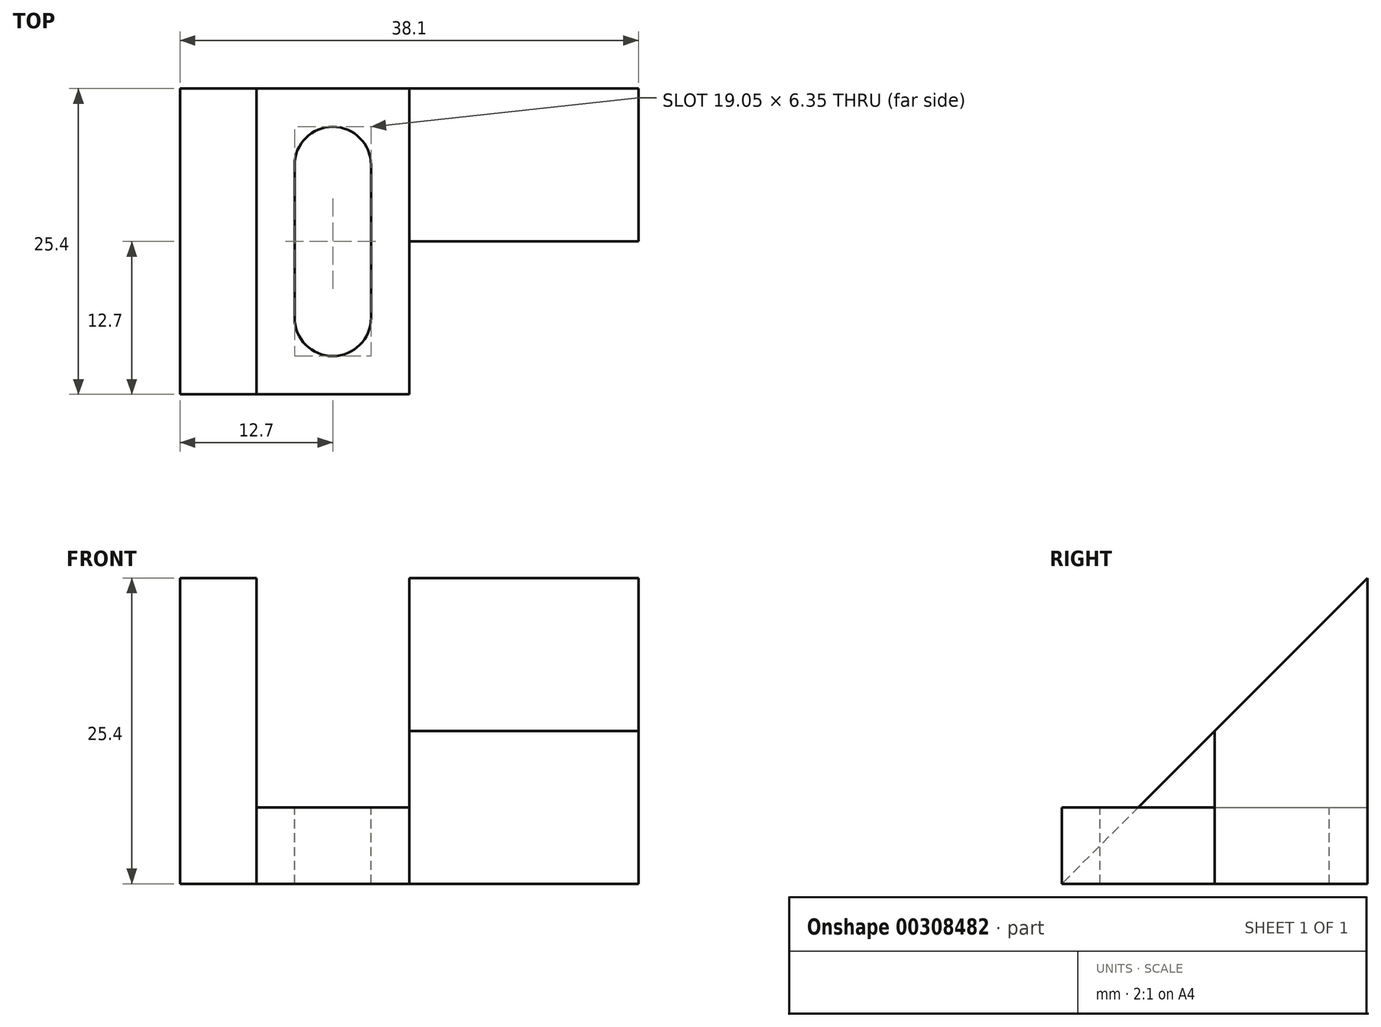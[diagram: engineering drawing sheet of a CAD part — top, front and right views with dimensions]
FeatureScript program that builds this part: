
annotation { "Feature Type Name" : "Feature", "Feature Type Description" : "" }
export const myFeature = defineFeature(function(context is Context, id is Id, definition is map)
    precondition{}
    {
        {
            var Q0;
            Q0=qCreatedBy(makeId("Right.planeOp"),FACE);
            var sketch = newSketch(context, id + "F0", { "sketchPlane" : qUnion([Q0])});
            skLineSegment(sketch, "E0", {"start": v(0, 0) * mm, "end": v(25.4, 0) * mm});
            skLineSegment(sketch, "E1", {"start": v(25.4, 0) * mm, "end": v(25.4, 25.4) * mm});
            skLineSegment(sketch, "E2", {"start": v(25.4, 25.4) * mm, "end": v(0, 0) * mm});
            skSolve(sketch);
        }
        {
            var Q0;
            Q0 = qSketchRegion(id + "F0", true);
            extrude(context, id + "F1", {"entities" : qUnion([Q0]), "oppositeDirection" : true, "depth" : 38.1 * mm});
        }
        {
            var Q0;
            Q0=makeQuery(id+"F1.opExtrude","CAP_FACE",FACE,{"disambiguationData":[OSD([sQuery(id+"F0.wireOp",EDGE,"E0"),sQuery(id+"F0.wireOp",EDGE,"E1"),sQuery(id+"F0.wireOp",EDGE,"E2")])],"isStart":true});
            var sketch = newSketch(context, id + "F2", { "sketchPlane" : qUnion([Q0])});
            skLineSegment(sketch, "E3", {"start": v(12.7, 0) * mm, "end": v(12.7, 12.7) * mm});
            skLineSegment(sketch, "E4", {"start": v(12.7, 12.7) * mm, "end": v(0, 0) * mm});
            skLineSegment(sketch, "E5", {"start": v(0, 0) * mm, "end": v(12.7, 0) * mm});
            skSolve(sketch);
        }
        {
            var Q0;
            Q0 = qSketchRegion(id + "F2", true);
            extrude(context, id + "F3", {"entities" : qUnion([Q0]), "operationType" : NewBodyOperationType.REMOVE, "oppositeDirection" : true, "depth" : 31.75 * mm});
        }
        {
            var Q0;
            Q0=makeQuery(id+"F1.opExtrude","SWEPT_FACE",FACE,{"disambiguationData":[OSD([sQuery(id+"F0.wireOp",EDGE,"E1")])]});
            var sketch = newSketch(context, id + "F4", { "sketchPlane" : qUnion([Q0])});
            skLineSegment(sketch, "E6", {"start": v(31.75, 25.4) * mm, "end": v(31.75, 6.35) * mm});
            skLineSegment(sketch, "E7", {"start": v(31.75, 6.35) * mm, "end": v(19.05, 6.35) * mm});
            skLineSegment(sketch, "E8", {"start": v(19.05, 6.35) * mm, "end": v(19.05, 25.4) * mm});
            skLineSegment(sketch, "E9", {"start": v(19.05, 25.4) * mm, "end": v(31.75, 25.4) * mm});
            skSolve(sketch);
        }
        {
            var Q0;
            Q0 = qSketchRegion(id + "F4", true);
            extrude(context, id + "F5", {"entities" : qUnion([Q0]), "operationType" : NewBodyOperationType.REMOVE, "oppositeDirection" : true, "depth" : 25.4 * mm});
        }
        {
            var Q0;
            Q0=makeQuery(id+"F1.opExtrude","SWEPT_FACE",FACE,{"disambiguationData":[OSD([sQuery(id+"F0.wireOp",EDGE,"E0")])]});
            var sketch = newSketch(context, id + "F6", { "sketchPlane" : qUnion([Q0])});
            skLineSegment(sketch, "E10", {"start": v(-31.75, -12.7) * mm, "end": v(-31.75, 0) * mm});
            skLineSegment(sketch, "E11", {"start": v(-31.75, 0) * mm, "end": v(-19.05, 0) * mm});
            skLineSegment(sketch, "E12", {"start": v(-19.05, 0) * mm, "end": v(-19.05, -12.7) * mm});
            skLineSegment(sketch, "E13", {"start": v(-19.05, -12.7) * mm, "end": v(-31.75, -12.7) * mm});
            skSolve(sketch);
        }
        {
            var Q0;
            Q0 = qSketchRegion(id + "F6", true);
            extrude(context, id + "F7", {"entities" : qUnion([Q0]), "operationType" : NewBodyOperationType.ADD, "oppositeDirection" : true, "depth" : 6.35 * mm});
        }
        {
            var Q0;
            Q0=makeQuery(id+"F7.boolean.opBoolean","MERGE",FACE,{"derivedFrom":[makeQuery(id+"F5.boolean.opBoolean","COPY",FACE,{"derivedFrom":makeQuery(id+"F5.opExtrude","SWEPT_FACE",FACE,{"disambiguationData":[OSD([sQuery(id+"F4.wireOp",EDGE,"E7")])]})}),makeQuery(id+"F7.opExtrude","CAP_FACE",FACE,{"disambiguationData":[OSD([sQuery(id+"F6.wireOp",EDGE,"E10"),sQuery(id+"F6.wireOp",EDGE,"E11"),sQuery(id+"F6.wireOp",EDGE,"E12"),sQuery(id+"F6.wireOp",EDGE,"E13")])],"isStart":false})]});
            var sketch = newSketch(context, id + "F8", { "sketchPlane" : qUnion([Q0])});
            skArc(sketch, "E14", {"start": v(-28.57, 6.35) * mm, "mid": v(-25.4, 3.18) * mm, "end": v(-22.22, 6.35) * mm});
            skPoint(sketch, "E14.centerSnap0", {"position": v(-25.4, 0) * mm});
            skArc(sketch, "E15", {"start": v(-22.23, 19.05) * mm, "mid": v(-25.4, 22.23) * mm, "end": v(-28.58, 19.05) * mm});
            skLineSegment(sketch, "E16", {"start": v(-28.57, 19.05) * mm, "end": v(-28.57, 6.35) * mm});
            skLineSegment(sketch, "E17", {"start": v(-22.22, 6.35) * mm, "end": v(-22.22, 19.05) * mm});
            skSolve(sketch);
        }
        {
            var Q0;
            Q0 = qSketchRegion(id + "F8", true);
            extrude(context, id + "F9", {"entities" : qUnion([Q0]), "operationType" : NewBodyOperationType.REMOVE, "oppositeDirection" : true, "depth" : 25.4 * mm});
        }
    });
